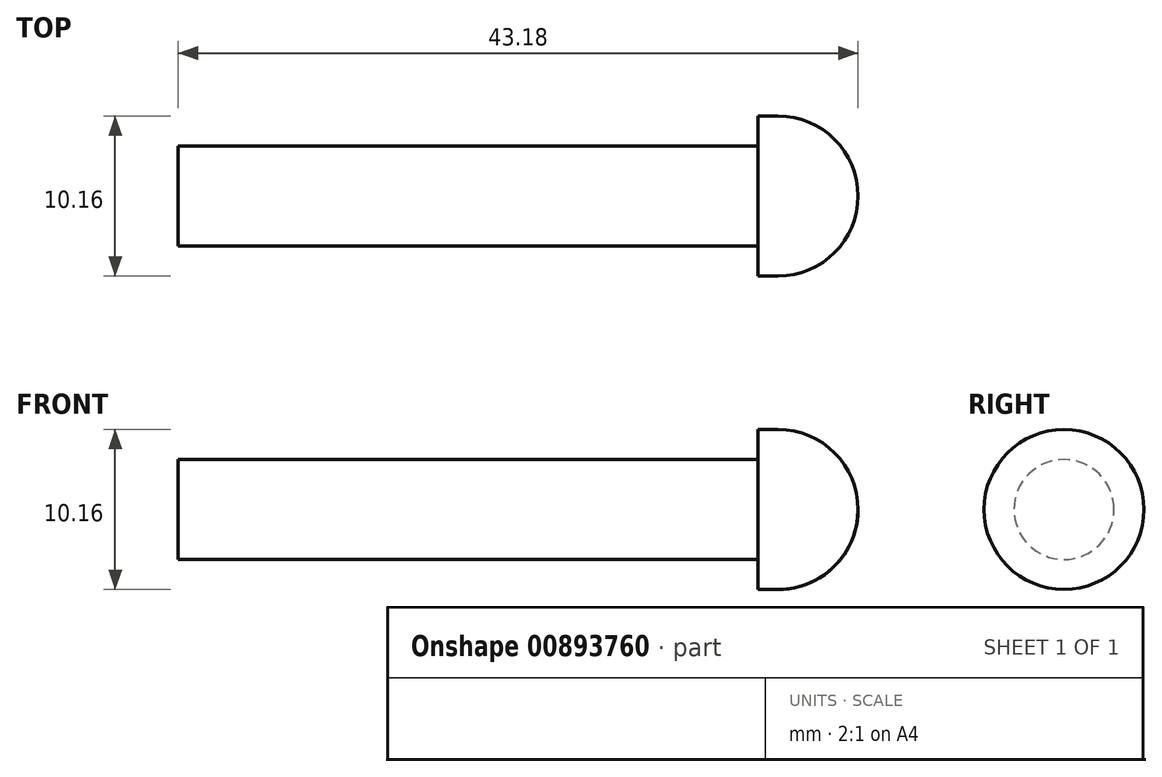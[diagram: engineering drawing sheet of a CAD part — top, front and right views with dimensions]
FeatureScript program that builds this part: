
annotation { "Feature Type Name" : "Feature", "Feature Type Description" : "" }
export const myFeature = defineFeature(function(context is Context, id is Id, definition is map)
    precondition{}
    {
        {
            var Q0;
            Q0=qCreatedBy(makeId("Right.planeOp"),FACE);
            var sketch = newSketch(context, id + "F0", { "sketchPlane" : qUnion([Q0])});
            skCircle(sketch, "E0", {"center": v(0, 0) * mm, "radius": 3.18 * mm});
            skSolve(sketch);
        }
        {
            var Q0;
            Q0 = qSketchRegion(id + "F0", true);
            extrude(context, id + "F1", {"entities" : qUnion([Q0]), "depth" : 36.83 * mm, "offsetDistance" : 25.4 * mm});
        }
        {
            var Q0;
            Q0=makeQuery(id+"F1.opExtrude","CAP_FACE",FACE,{"disambiguationData":[OSD([sQuery(id+"F0.wireOp",EDGE,"E0")])],"isStart":false});
            var sketch = newSketch(context, id + "F2", { "sketchPlane" : qUnion([Q0])});
            skCircle(sketch, "E1", {"center": v(0, 0) * mm, "radius": 5.08 * mm});
            skSolve(sketch);
        }
        {
            var Q0;
            Q0 = qSketchRegion(id + "F2", true);
            extrude(context, id + "F3", {"entities" : qUnion([Q0]), "operationType" : NewBodyOperationType.ADD, "depth" : 6.35 * mm, "offsetDistance" : 25.4 * mm});
        }
        {
            var Q0;
            Q0=makeQuery(id+"F3.opExtrude","CAP_EDGE",EDGE,{"disambiguationData":[OSD([sQuery(id+"F2.wireOp",EDGE,"E1")])],"isStart":false});
            fillet(context, id + "F4", {"entities" : qUnion([Q0]), "radius" : 5.08 * mm, "tangentPropagation" : true, "allowEdgeOverflow" : false});
        }
    });
